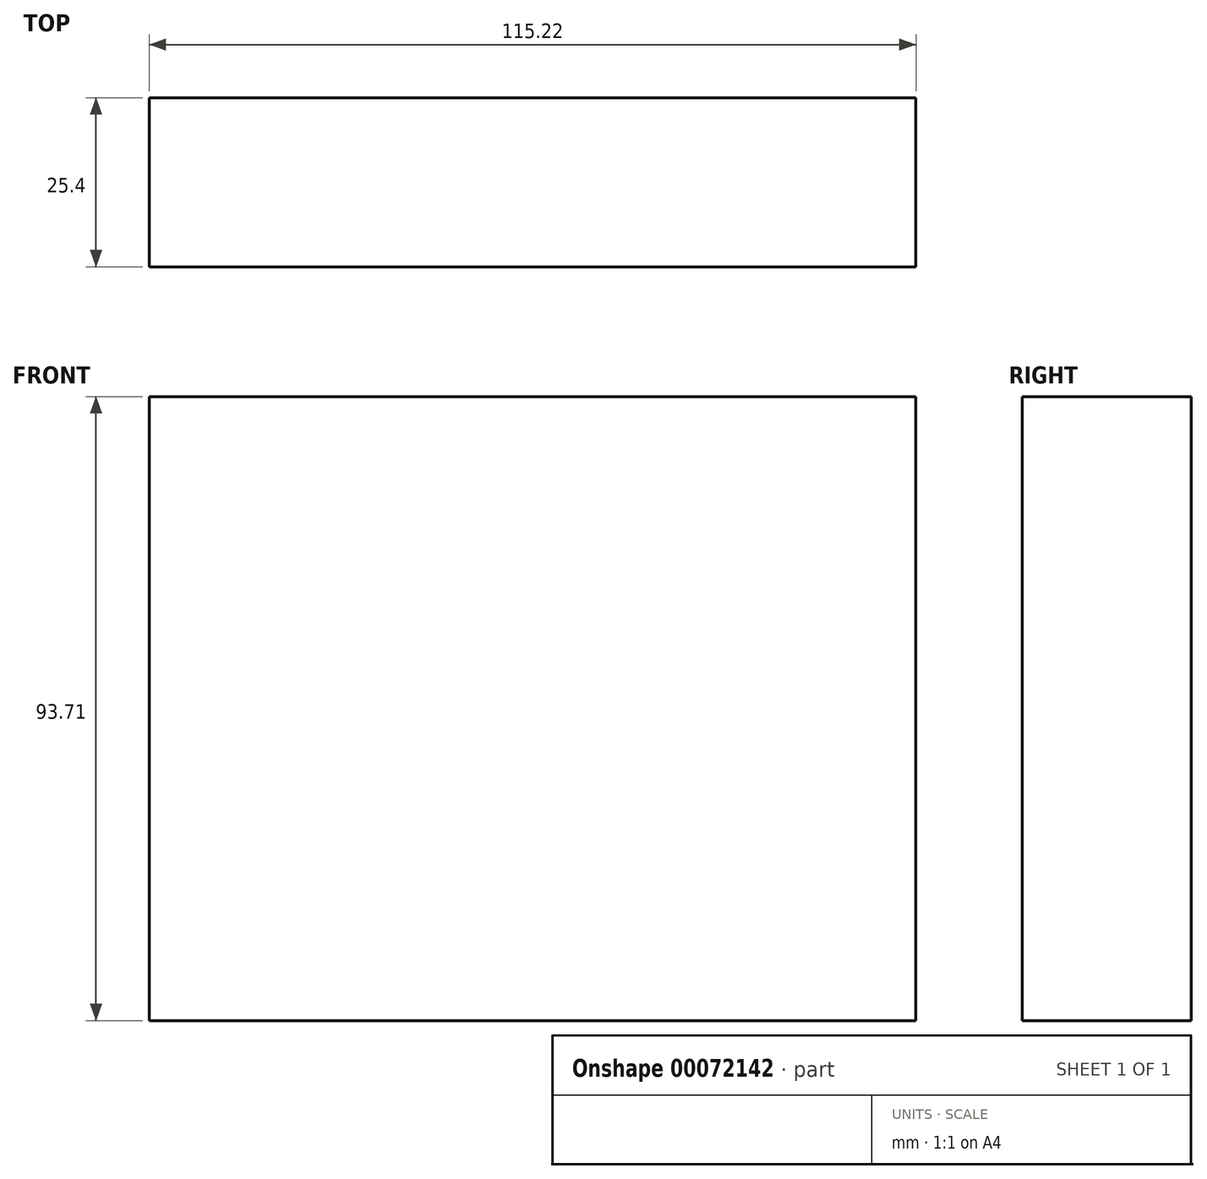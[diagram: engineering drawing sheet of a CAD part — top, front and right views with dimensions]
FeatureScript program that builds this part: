
annotation { "Feature Type Name" : "Feature", "Feature Type Description" : "" }
export const myFeature = defineFeature(function(context is Context, id is Id, definition is map)
    precondition{}
    {
        {
            var Q0;
            Q0=qCreatedBy(makeId("Front.planeOp"),FACE);
            var sketch = newSketch(context, id + "F0", { "sketchPlane" : qUnion([Q0])});
            skLineSegment(sketch, "E0.bottom", {"start": v(57.6, 36.96) * mm, "end": v(-57.6, 36.96) * mm});
            skLineSegment(sketch, "E0.top", {"start": v(57.6, -36.96) * mm, "end": v(-57.6, -36.96) * mm});
            skLineSegment(sketch, "E0.left", {"start": v(57.6, 36.96) * mm, "end": v(57.6, -36.96) * mm});
            skLineSegment(sketch, "E0.right", {"start": v(-57.6, 36.96) * mm, "end": v(-57.6, -36.96) * mm});
            skPoint(sketch, "E0.middle", {"position": v(0, 0) * mm});
            skLineSegment(sketch, "E1", {"start": v(57.6, 36.96) * mm, "end": v(57.6, 56.75) * mm});
            skLineSegment(sketch, "E2", {"start": v(-57.6, 36.96) * mm, "end": v(-57.6, 56.75) * mm});
            skLineSegment(sketch, "E3", {"start": v(-57.6, 56.75) * mm, "end": v(57.6, 56.75) * mm});
            skSolve(sketch);
        }
        {
            var Q0;
            Q0=makeQuery(id+"F0.imprint","IMPRINT",FACE,{"disambiguationData":[TD([[makeQuery(id+"F0.imprint","IMPRINT",EDGE,{"derivedFrom":sQuery(id+"F0.wireOp",EDGE,"E0.bottom")}),1.0]])]});
            var Q1;
            Q1=makeQuery(id+"F0.imprint","IMPRINT",FACE,{"disambiguationData":[TD([[makeQuery(id+"F0.imprint","IMPRINT",EDGE,{"derivedFrom":sQuery(id+"F0.wireOp",EDGE,"E0.bottom")}),-1.0]])]});
            extrude(context, id + "F1", {"entities" : qUnion([Q0, Q1]), "depth" : 25.4 * mm});
        }
    });
